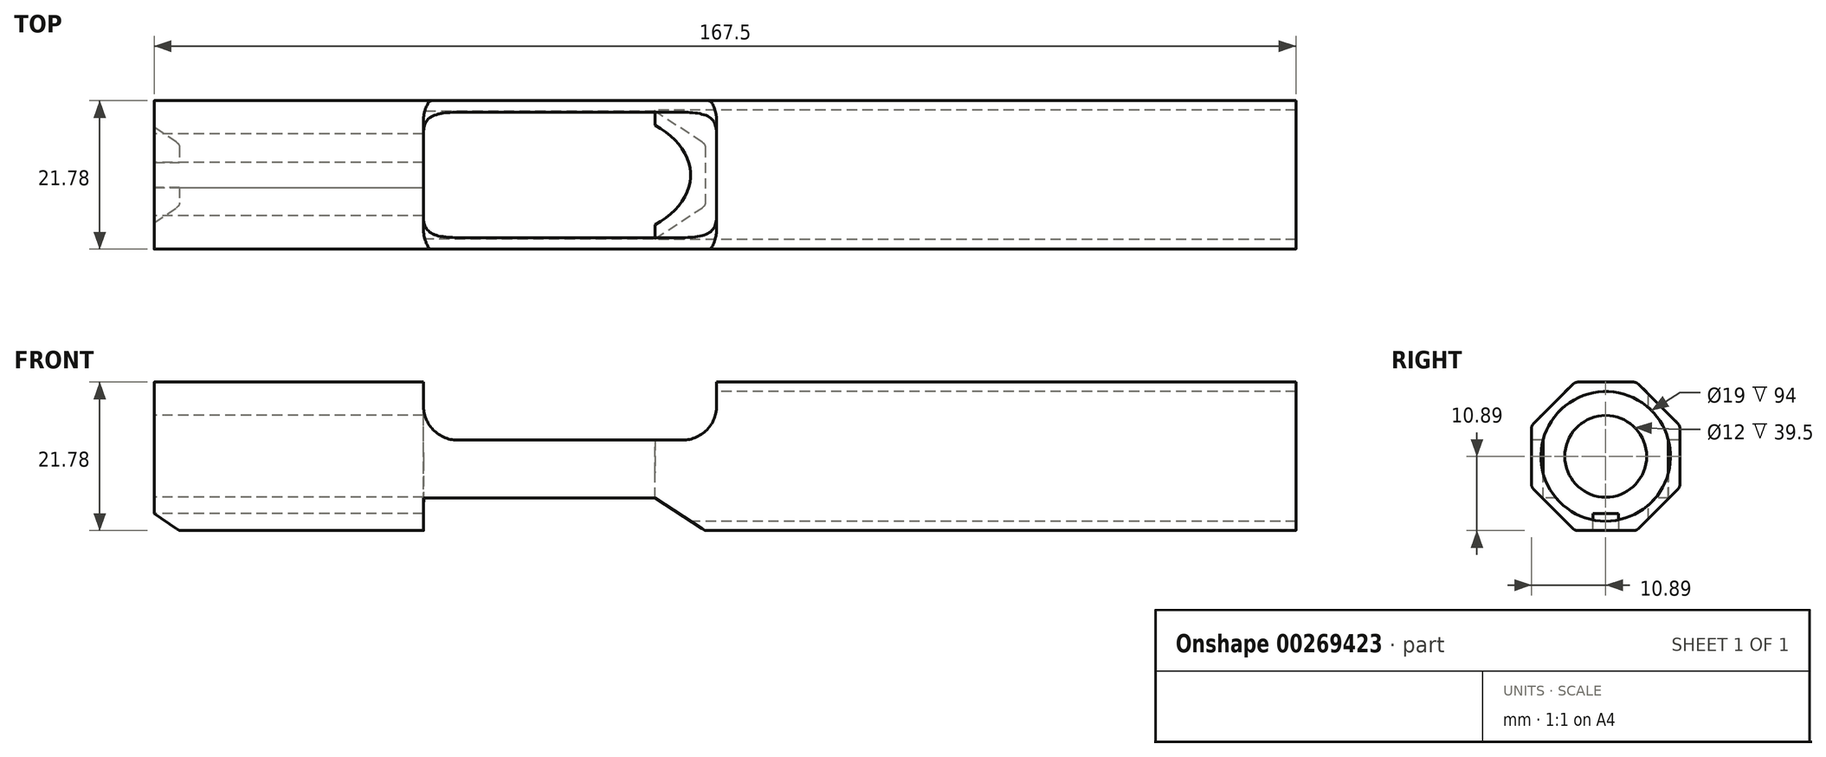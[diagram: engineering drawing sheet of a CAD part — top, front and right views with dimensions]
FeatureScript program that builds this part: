
annotation { "Feature Type Name" : "Feature", "Feature Type Description" : "" }
export const myFeature = defineFeature(function(context is Context, id is Id, definition is map)
    precondition{}
    {
        {
            var Q0;
            Q0=qCreatedBy(makeId("Right.planeOp"),FACE);
            var sketch = newSketch(context, id + "F0", { "sketchPlane" : qUnion([Q0])});
            skLineSegment(sketch, "E0", {"start": v(-17.38, 0) * mm, "end": v(17.63, 0) * mm, "construction": true});
            skLineSegment(sketch, "E1", {"start": v(0, 17.45) * mm, "end": v(0, -16.93) * mm, "construction": true});
            skCircle(sketch, "E2.cCircle", {"center": v(0, 0) * mm, "radius": 10.89 * mm, "construction": true});
            skLineSegment(sketch, "E2.0", {"start": v(4.1, -10.89) * mm, "end": v(-4.1, -10.89) * mm});
            skLineSegment(sketch, "E2.1", {"start": v(-4.8, -10.6) * mm, "end": v(-10.6, -4.8) * mm});
            skLineSegment(sketch, "E2.2", {"start": v(-10.89, -4.1) * mm, "end": v(-10.89, 4.1) * mm});
            skLineSegment(sketch, "E2.3", {"start": v(-10.6, 4.8) * mm, "end": v(-4.8, 10.6) * mm});
            skLineSegment(sketch, "E2.4", {"start": v(-4.1, 10.89) * mm, "end": v(4.1, 10.89) * mm});
            skLineSegment(sketch, "E2.5", {"start": v(4.8, 10.6) * mm, "end": v(10.6, 4.8) * mm});
            skLineSegment(sketch, "E2.6", {"start": v(10.89, 4.1) * mm, "end": v(10.89, -4.1) * mm});
            skLineSegment(sketch, "E2.7", {"start": v(10.6, -4.8) * mm, "end": v(4.8, -10.6) * mm});
            skPoint(sketch, "E2.0.midPoint", {"position": v(0, -10.89) * mm});
            skLineSegment(sketch, "E3", {"start": v(4.51, 11.35) * mm, "end": v(-4.51, -10.89) * mm, "construction": true});
            skCircle(sketch, "E4", {"center": v(0, 0) * mm, "radius": 9.5 * mm});
            skPoint(sketch, "E5.visualSharp", {"position": v(-4.51, 10.89) * mm});
            skArc(sketch, "E5.filletArc", {"start": v(-4.1, 10.89) * mm, "mid": v(-4.48, 10.81) * mm, "end": v(-4.8, 10.6) * mm});
            skPoint(sketch, "E6.visualSharp", {"position": v(4.51, 10.89) * mm});
            skArc(sketch, "E6.filletArc", {"start": v(4.8, 10.6) * mm, "mid": v(4.48, 10.81) * mm, "end": v(4.1, 10.89) * mm});
            skPoint(sketch, "E7.visualSharp", {"position": v(10.89, 4.51) * mm});
            skArc(sketch, "E7.filletArc", {"start": v(10.89, 4.1) * mm, "mid": v(10.81, 4.48) * mm, "end": v(10.6, 4.8) * mm});
            skPoint(sketch, "E8.visualSharp", {"position": v(10.89, -4.51) * mm});
            skArc(sketch, "E8.filletArc", {"start": v(10.6, -4.8) * mm, "mid": v(10.81, -4.48) * mm, "end": v(10.89, -4.1) * mm});
            skPoint(sketch, "E9.visualSharp", {"position": v(4.51, -10.89) * mm});
            skArc(sketch, "E9.filletArc", {"start": v(4.1, -10.89) * mm, "mid": v(4.48, -10.81) * mm, "end": v(4.8, -10.6) * mm});
            skPoint(sketch, "E10.visualSharp", {"position": v(-4.51, -10.89) * mm});
            skArc(sketch, "E10.filletArc", {"start": v(-4.8, -10.6) * mm, "mid": v(-4.48, -10.81) * mm, "end": v(-4.1, -10.89) * mm});
            skPoint(sketch, "E11.visualSharp", {"position": v(-10.89, -4.51) * mm});
            skArc(sketch, "E11.filletArc", {"start": v(-10.89, -4.1) * mm, "mid": v(-10.81, -4.48) * mm, "end": v(-10.6, -4.8) * mm});
            skPoint(sketch, "E12.visualSharp", {"position": v(-10.89, 4.51) * mm});
            skArc(sketch, "E12.filletArc", {"start": v(-10.6, 4.8) * mm, "mid": v(-10.81, 4.48) * mm, "end": v(-10.89, 4.1) * mm});
            skSolve(sketch);
        }
        {
            var Q0;
            Q0 = qSketchRegion(id + "F0", true);
            extrude(context, id + "F1", {"entities" : qUnion([Q0]), "endBound" : BoundingType.SYMMETRIC, "depth" : 167.5 * mm});
        }
        {
            var Q0;
            Q0=qCreatedBy(makeId("Front.planeOp"),FACE);
            var sketch = newSketch(context, id + "F2", { "sketchPlane" : qUnion([Q0])});
            skLineSegment(sketch, "E13.0", {"start": v(83.75, 10.89) * mm, "end": v(-83.75, 10.89) * mm, "construction": true});
            skLineSegment(sketch, "E14.0", {"start": v(83.75, -10.89) * mm, "end": v(-83.75, -10.89) * mm, "construction": true});
            skPoint(sketch, "E15.0", {"position": v(0, 0) * mm});
            skLineSegment(sketch, "E16", {"start": v(0, 0) * mm, "end": v(-87.86, 0) * mm, "construction": true});
            skLineSegment(sketch, "E17", {"start": v(0, 33.1) * mm, "end": v(0, -22.97) * mm, "construction": true});
            skLineSegment(sketch, "E18.0", {"start": v(-83.75, 10.6) * mm, "end": v(-83.75, 4.8) * mm, "construction": true});
            skLineSegment(sketch, "E19.0", {"start": v(-83.75, 4.1) * mm, "end": v(-83.75, -4.1) * mm, "construction": true});
            skLineSegment(sketch, "E20.0", {"start": v(-83.75, -4.8) * mm, "end": v(-83.75, -10.6) * mm, "construction": true});
            skLineSegment(sketch, "E21.0", {"start": v(-83.75, -10.89) * mm, "end": v(-83.75, -10.6) * mm, "construction": true});
            skLineSegment(sketch, "E22.0", {"start": v(-83.75, 10.6) * mm, "end": v(-83.75, 10.89) * mm, "construction": true});
            skLineSegment(sketch, "E23.bottom", {"start": v(-1.25, 10.89) * mm, "end": v(-44.25, 10.89) * mm});
            skLineSegment(sketch, "E23.top", {"start": v(-6.25, 2.39) * mm, "end": v(-39.25, 2.39) * mm});
            skLineSegment(sketch, "E23.left", {"start": v(-1.25, 10.89) * mm, "end": v(-1.25, 7.39) * mm});
            skLineSegment(sketch, "E23.right", {"start": v(-44.25, 10.89) * mm, "end": v(-44.25, 7.39) * mm});
            skPoint(sketch, "E24.visualSharp", {"position": v(-44.25, 2.39) * mm});
            skArc(sketch, "E24.filletArc", {"start": v(-44.25, 7.39) * mm, "mid": v(-42.79, 3.85) * mm, "end": v(-39.25, 2.39) * mm});
            skPoint(sketch, "E25.visualSharp", {"position": v(-1.25, 2.39) * mm});
            skArc(sketch, "E25.filletArc", {"start": v(-6.25, 2.39) * mm, "mid": v(-2.71, 3.85) * mm, "end": v(-1.25, 7.39) * mm});
            skLineSegment(sketch, "E26.bottom", {"start": v(-44.25, -10.89) * mm, "end": v(-2.9, -10.89) * mm});
            skLineSegment(sketch, "E26.top", {"start": v(-44.25, -6.09) * mm, "end": v(-10.25, -6.09) * mm});
            skLineSegment(sketch, "E26.left", {"start": v(-44.25, -10.89) * mm, "end": v(-44.25, -6.09) * mm});
            skLineSegment(sketch, "E27", {"start": v(-10.25, -6.09) * mm, "end": v(-2.9, -10.89) * mm});
            skLineSegment(sketch, "E28", {"start": v(-2.9, -10.89) * mm, "end": v(-44.25, -10.89) * mm});
            skLineSegment(sketch, "E29", {"start": v(-10.25, -6.09) * mm, "end": v(-44.25, -6.09) * mm});
            skSolve(sketch);
        }
        {
            var Q0;
            Q0 = qSketchRegion(id + "F2", true);
            extrude(context, id + "F3", {"entities" : qUnion([Q0]), "operationType" : NewBodyOperationType.REMOVE, "endBound" : BoundingType.SYMMETRIC, "oppositeDirection" : true, "depth" : 25 * mm});
        }
        {
            var Q0;
            Q0=makeQuery(id+"F1.opExtrude","CAP_FACE",FACE,{"disambiguationData":[OSD([sQuery(id+"F0.wireOp",EDGE,"E2.0"),sQuery(id+"F0.wireOp",EDGE,"E2.1"),sQuery(id+"F0.wireOp",EDGE,"E2.2"),sQuery(id+"F0.wireOp",EDGE,"E2.3"),sQuery(id+"F0.wireOp",EDGE,"E2.4"),sQuery(id+"F0.wireOp",EDGE,"E2.5"),sQuery(id+"F0.wireOp",EDGE,"E2.6"),sQuery(id+"F0.wireOp",EDGE,"E2.7"),sQuery(id+"F0.wireOp",EDGE,"E4"),sQuery(id+"F0.wireOp",EDGE,"E5.filletArc"),sQuery(id+"F0.wireOp",EDGE,"E6.filletArc"),sQuery(id+"F0.wireOp",EDGE,"E7.filletArc"),sQuery(id+"F0.wireOp",EDGE,"E8.filletArc"),sQuery(id+"F0.wireOp",EDGE,"E9.filletArc"),sQuery(id+"F0.wireOp",EDGE,"E10.filletArc"),sQuery(id+"F0.wireOp",EDGE,"E11.filletArc"),sQuery(id+"F0.wireOp",EDGE,"E12.filletArc")])],"isStart":true});
            cPlane(context, id + "F4", {"entities" : qUnion([Q0]), "cplaneType" : CPlaneType.OFFSET, "offset" : 0 * mm, "width" : 150 * mm, "height" : 150 * mm});
        }
        {
            var Q0;
            Q0=qCreatedBy(id+"F4.planeOp",FACE);
            var sketch = newSketch(context, id + "F5", { "sketchPlane" : qUnion([Q0])});
            skCircle(sketch, "E30.0", {"center": v(0, 0) * mm, "radius": 9.5 * mm, "construction": true});
            skPoint(sketch, "E31", {"position": v(0, 9.5) * mm});
            skCircle(sketch, "E32", {"center": v(0, 0) * mm, "radius": 9.5 * mm});
            skCircle(sketch, "E33", {"center": v(0, 0) * mm, "radius": 6 * mm});
            skSolve(sketch);
        }
        {
            var Q0;
            Q0 = qSketchRegion(id + "F5", true);
            extrude(context, id + "F6", {"entities" : qUnion([Q0]), "operationType" : NewBodyOperationType.ADD, "oppositeDirection" : true, "depth" : 73.5 * mm});
        }
        {
            var Q0;
            Q0=qCreatedBy(makeId("Top.planeOp"),FACE);
            var sketch = newSketch(context, id + "F7", { "sketchPlane" : qUnion([Q0])});
            skLineSegment(sketch, "E34.0.0", {"start": v(-10.25, -9.2) * mm, "end": v(-10.25, 9.2) * mm});
            skLineSegment(sketch, "E34.0.1", {"start": v(-10.25, 9.2) * mm, "end": v(-39.25, 9.2) * mm});
            skFitSpline(sketch, "E34.0.2", {"points": [v(-39.25, 9.2) * mm, v(-39.62, 9.2) * mm, v(-40.35, 9.17) * mm, v(-41.23, 9.09) * mm, v(-41.86, 8.98) * mm, v(-42.31, 8.86) * mm, v(-42.72, 8.72) * mm, v(-43.2, 8.5) * mm, v(-43.67, 8.1) * mm, v(-43.97, 7.62) * mm, v(-44.13, 7.16) * mm, v(-44.23, 6.67) * mm, v(-44.25, 6.26) * mm, v(-44.25, 5.97) * mm]});
            skLineSegment(sketch, "E34.0.3", {"start": v(-44.25, 5.97) * mm, "end": v(-44.25, -5.97) * mm});
            skFitSpline(sketch, "E34.0.4", {"points": [v(-44.25, -5.97) * mm, v(-44.25, -6.26) * mm, v(-44.22, -6.8) * mm, v(-44.06, -7.4) * mm, v(-43.85, -7.82) * mm, v(-43.64, -8.1) * mm, v(-43.38, -8.34) * mm, v(-43.07, -8.55) * mm, v(-42.71, -8.72) * mm, v(-42.3, -8.87) * mm, v(-41.86, -8.98) * mm, v(-41.38, -9.06) * mm, v(-40.87, -9.12) * mm, v(-40.16, -9.18) * mm, v(-39.62, -9.2) * mm, v(-39.25, -9.2) * mm]});
            skLineSegment(sketch, "E34.0.5", {"start": v(-39.25, -9.2) * mm, "end": v(-10.25, -9.2) * mm});
            skSolve(sketch);
        }
        {
            var Q0;
            Q0 = qSketchRegion(id + "F7", true);
            extrude(context, id + "F8", {"entities" : qUnion([Q0]), "operationType" : NewBodyOperationType.REMOVE, "endBound" : BoundingType.SYMMETRIC, "oppositeDirection" : true, "depth" : 25 * mm});
        }
        {
            var Q0;
            {var subQ2=sQuery(id+"F0.wireOp",EDGE,"E2.0");Q0=makeQuery(id+"F3.boolean.opBoolean","SPLIT",FACE,{"disambiguationData":[TD([makeQuery(id+"F3.opExtrude","SWEPT_FACE",FACE,{"disambiguationData":[OSD([sQuery(id+"F2.wireOp",EDGE,"E26.left")])]})])],"derivedFrom":makeQuery(id+"F1.opExtrude","SWEPT_FACE",FACE,{"disambiguationData":[OSD([subQ2])]})});}
            cPlane(context, id + "F9", {"entities" : qUnion([Q0]), "cplaneType" : CPlaneType.OFFSET, "offset" : 0 * mm, "width" : 150 * mm, "height" : 150 * mm});
        }
        {
            var Q0;
            Q0=qCreatedBy(makeId("Top.planeOp"),FACE);
            var sketch = newSketch(context, id + "F10", { "sketchPlane" : qUnion([Q0])});
            skLineSegment(sketch, "E35", {"start": v(0, 0) * mm, "end": v(-92.83, 0) * mm, "construction": true});
            skLineSegment(sketch, "E36.bottom", {"start": v(-60.83, -1.85) * mm, "end": v(-92.83, -1.85) * mm});
            skLineSegment(sketch, "E36.top", {"start": v(-60.83, 1.85) * mm, "end": v(-92.83, 1.85) * mm});
            skLineSegment(sketch, "E37", {"start": v(-60.83, -1.85) * mm, "end": v(-38.13, -1.85) * mm});
            skLineSegment(sketch, "E38", {"start": v(-38.13, -1.85) * mm, "end": v(-38.13, 1.85) * mm});
            skLineSegment(sketch, "E39", {"start": v(-38.13, 1.85) * mm, "end": v(-59.24, 1.85) * mm});
            skLineSegment(sketch, "E40", {"start": v(-60.83, 1.85) * mm, "end": v(-59.24, 1.85) * mm});
            skLineSegment(sketch, "E41", {"start": v(-92.83, -1.85) * mm, "end": v(-92.83, 1.85) * mm});
            skSolve(sketch);
        }
        {
            var Q0;
            Q0=qCreatedBy(id+"F9.planeOp",FACE);
            var sketch = newSketch(context, id + "F11", { "sketchPlane" : qUnion([Q0])});
            skLineSegment(sketch, "E42.0.0", {"start": v(-59.24, -1.85) * mm, "end": v(-60.83, -1.85) * mm});
            skLineSegment(sketch, "E42.0.1", {"start": v(-60.83, -1.85) * mm, "end": v(-92.83, -1.85) * mm});
            skLineSegment(sketch, "E42.0.2", {"start": v(-92.83, -1.85) * mm, "end": v(-92.83, 1.85) * mm});
            skLineSegment(sketch, "E42.0.3", {"start": v(-92.83, 1.85) * mm, "end": v(-60.83, 1.85) * mm});
            skLineSegment(sketch, "E42.0.4", {"start": v(-60.83, 1.85) * mm, "end": v(-38.13, 1.85) * mm});
            skLineSegment(sketch, "E42.0.5", {"start": v(-38.13, 1.85) * mm, "end": v(-38.13, -1.85) * mm});
            skLineSegment(sketch, "E42.0.6", {"start": v(-38.13, -1.85) * mm, "end": v(-59.24, -1.85) * mm});
            skSolve(sketch);
        }
        {
            var Q0;
            Q0 = qSketchRegion(id + "F11", true);
            extrude(context, id + "F12", {"entities" : qUnion([Q0]), "operationType" : NewBodyOperationType.REMOVE, "oppositeDirection" : true, "depth" : 2.5 * mm});
        }
        {
            var Q0;
            Q0=makeQuery(id+"F1.opExtrude","SWEPT_FACE",FACE,{"disambiguationData":[OSD([sQuery(id+"F0.wireOp",EDGE,"E2.2")])]});
            cPlane(context, id + "F13", {"entities" : qUnion([Q0]), "cplaneType" : CPlaneType.OFFSET, "offset" : 25 * mm, "width" : 150 * mm, "height" : 150 * mm});
        }
        {
            var Q0;
            Q0=qCreatedBy(id+"F13.planeOp",FACE);
            var sketch = newSketch(context, id + "F14", { "sketchPlane" : qUnion([Q0])});
            skLineSegment(sketch, "E43.0", {"start": v(83.75, -10.89) * mm, "end": v(-80.05, -10.89) * mm});
            skLineSegment(sketch, "E44.0", {"start": v(-83.75, -4.8) * mm, "end": v(-83.75, -9.37) * mm});
            skPoint(sketch, "E45.start.orphan", {"position": v(-80.05, -10.6) * mm});
            skPoint(sketch, "E46.orphan", {"position": v(-83.75, -10.6) * mm});
            skPoint(sketch, "E47.0.start.orphan", {"position": v(-83.75, -10.89) * mm});
            skLineSegment(sketch, "E48", {"start": v(-83.75, -9.37) * mm, "end": v(-83.75, -10.89) * mm});
            skLineSegment(sketch, "E49", {"start": v(-83.75, -10.89) * mm, "end": v(-80.05, -10.89) * mm});
            skLineSegment(sketch, "E50.0", {"start": v(-83.75, -10.89) * mm, "end": v(-83.75, -8.39) * mm, "construction": true});
            skPoint(sketch, "E51.0", {"position": v(-83.75, -8.39) * mm});
            skLineSegment(sketch, "E52", {"start": v(-80.05, -10.89) * mm, "end": v(-83.75, -10.89) * mm});
            skLineSegment(sketch, "E53", {"start": v(-83.75, -8.39) * mm, "end": v(-80.05, -10.89) * mm});
            skSolve(sketch);
        }
        {
            var Q0;
            Q0 = qSketchRegion(id + "F14", true);
            extrude(context, id + "F15", {"entities" : qUnion([Q0]), "operationType" : NewBodyOperationType.REMOVE, "endBound" : BoundingType.THROUGH_ALL, "oppositeDirection" : true, "depth" : 25 * mm});
        }
    });
